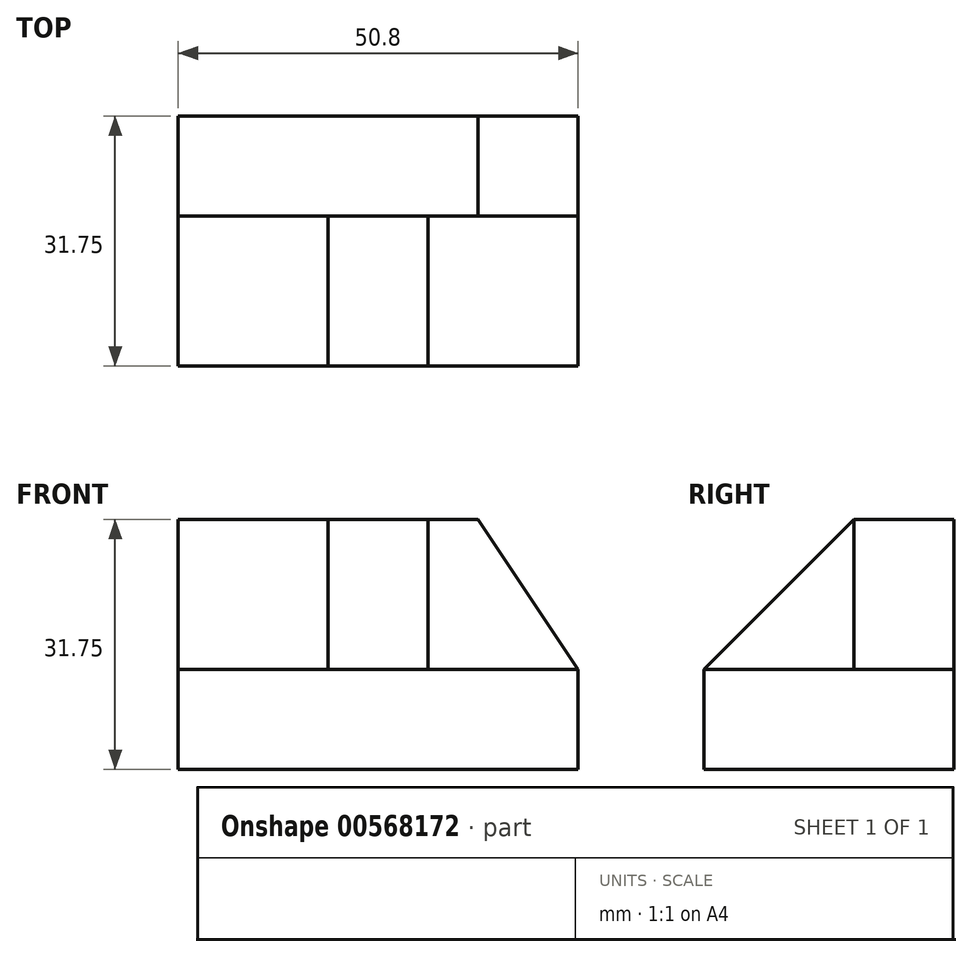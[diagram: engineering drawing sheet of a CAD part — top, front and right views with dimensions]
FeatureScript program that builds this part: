
annotation { "Feature Type Name" : "Feature", "Feature Type Description" : "" }
export const myFeature = defineFeature(function(context is Context, id is Id, definition is map)
    precondition{}
    {
        {
            var Q0;
            Q0=qCreatedBy(makeId("Front.planeOp"),FACE);
            var sketch = newSketch(context, id + "F0", { "sketchPlane" : qUnion([Q0])});
            skLineSegment(sketch, "E0", {"start": v(-62.9, 58.4) * mm, "end": v(-62.9, 26.66) * mm});
            skLineSegment(sketch, "E1", {"start": v(-62.9, 26.66) * mm, "end": v(-12.1, 26.66) * mm});
            skLineSegment(sketch, "E2", {"start": v(-12.1, 26.66) * mm, "end": v(-12.1, 58.4) * mm});
            skLineSegment(sketch, "E3", {"start": v(-12.1, 58.4) * mm, "end": v(-62.9, 58.4) * mm});
            skSolve(sketch);
        }
        {
            var Q0;
            Q0=makeQuery(id+"F0.imprint","IMPRINT",FACE,{"disambiguationData":[TD([[makeQuery(id+"F0.imprint","IMPRINT",EDGE,{"derivedFrom":sQuery(id+"F0.wireOp",EDGE,"E0")}),1.0]])]});
            extrude(context, id + "F1", {"entities" : qUnion([Q0]), "depth" : 31.75 * mm, "offsetDistance" : 25.4 * mm});
        }
        {
            var Q0;
            Q0=makeQuery(id+"F1.opExtrude","CAP_FACE",FACE,{"disambiguationData":[OSD([sQuery(id+"F0.wireOp",EDGE,"E0"),sQuery(id+"F0.wireOp",EDGE,"E1"),sQuery(id+"F0.wireOp",EDGE,"E2"),sQuery(id+"F0.wireOp",EDGE,"E3")])],"isStart":false});
            var sketch = newSketch(context, id + "F2", { "sketchPlane" : qUnion([Q0])});
            skLineSegment(sketch, "E4", {"start": v(-24.8, 58.4) * mm, "end": v(-12.1, 39.36) * mm});
            skSolve(sketch);
        }
        {
            var Q0;
            {var subQ0=sQuery(id+"F2.wireOp",EDGE,"E4");Q0=makeQuery(id+"F2.imprint","IMPRINT",FACE,{"disambiguationData":[TD([[makeQuery(id+"F2.imprint","IMPRINT",EDGE,{"derivedFrom":subQ0}),1.0]])]});}
            extrude(context, id + "F3", {"entities" : qUnion([Q0]), "operationType" : NewBodyOperationType.REMOVE, "oppositeDirection" : true, "depth" : 31.75 * mm, "offsetDistance" : 25.4 * mm});
        }
        {
            var Q0;
            Q0=makeQuery(id+"F1.opExtrude","CAP_FACE",FACE,{"disambiguationData":[OSD([sQuery(id+"F0.wireOp",EDGE,"E0"),sQuery(id+"F0.wireOp",EDGE,"E1"),sQuery(id+"F0.wireOp",EDGE,"E2"),sQuery(id+"F0.wireOp",EDGE,"E3")])],"isStart":false});
            var sketch = newSketch(context, id + "F4", { "sketchPlane" : qUnion([Q0])});
            skLineSegment(sketch, "E5", {"start": v(-31.16, 58.4) * mm, "end": v(-31.16, 39.36) * mm});
            skLineSegment(sketch, "E6", {"start": v(-31.16, 39.36) * mm, "end": v(-12.1, 39.36) * mm});
            skSolve(sketch);
        }
        {
            var Q0;
            {var subQ0=sQuery(id+"F4.wireOp",EDGE,"E5");Q0=makeQuery(id+"F4.imprint","IMPRINT",FACE,{"disambiguationData":[TD([[makeQuery(id+"F4.imprint","IMPRINT",EDGE,{"derivedFrom":subQ0}),1.0]])]});}
            extrude(context, id + "F5", {"entities" : qUnion([Q0]), "operationType" : NewBodyOperationType.REMOVE, "oppositeDirection" : true, "depth" : 19.05 * mm, "offsetDistance" : 25.4 * mm});
        }
        {
            var Q0;
            Q0=makeQuery(id+"F5.boolean.opBoolean","COPY",FACE,{"derivedFrom":makeQuery(id+"F5.opExtrude","SWEPT_FACE",FACE,{"disambiguationData":[OSD([sQuery(id+"F4.wireOp",EDGE,"E5")])]})});
            var sketch = newSketch(context, id + "F6", { "sketchPlane" : qUnion([Q0])});
            skLineSegment(sketch, "E7", {"start": v(-12.7, 58.4) * mm, "end": v(-31.75, 39.36) * mm});
            skSolve(sketch);
        }
        {
            var Q0;
            Q0=makeQuery(id+"F6.imprint","IMPRINT",FACE,{"disambiguationData":[TD([[makeQuery(id+"F6.imprint","IMPRINT",EDGE,{"derivedFrom":sQuery(id+"F6.wireOp",EDGE,"E7")}),-1.0]])]});
            extrude(context, id + "F7", {"entities" : qUnion([Q0]), "operationType" : NewBodyOperationType.REMOVE, "oppositeDirection" : true, "depth" : 31.75 * mm, "offsetDistance" : 25.4 * mm});
        }
        {
            var Q0;
            Q0=makeQuery(id+"F1.opExtrude","SWEPT_FACE",FACE,{"disambiguationData":[OSD([sQuery(id+"F0.wireOp",EDGE,"E0")])]});
            var sketch = newSketch(context, id + "F8", { "sketchPlane" : qUnion([Q0])});
            skLineSegment(sketch, "E8", {"start": v(12.7, 58.4) * mm, "end": v(12.7, 39.36) * mm});
            skLineSegment(sketch, "E9", {"start": v(12.7, 39.36) * mm, "end": v(31.75, 39.36) * mm});
            skSolve(sketch);
        }
        {
            var Q0;
            Q0=makeQuery(id+"F8.imprint","IMPRINT",FACE,{"disambiguationData":[TD([[makeQuery(id+"F8.imprint","IMPRINT",EDGE,{"derivedFrom":sQuery(id+"F8.wireOp",EDGE,"E8")}),1.0]])]});
            extrude(context, id + "F9", {"entities" : qUnion([Q0]), "operationType" : NewBodyOperationType.REMOVE, "oppositeDirection" : true, "depth" : 19.05 * mm, "offsetDistance" : 25.4 * mm});
        }
    });
